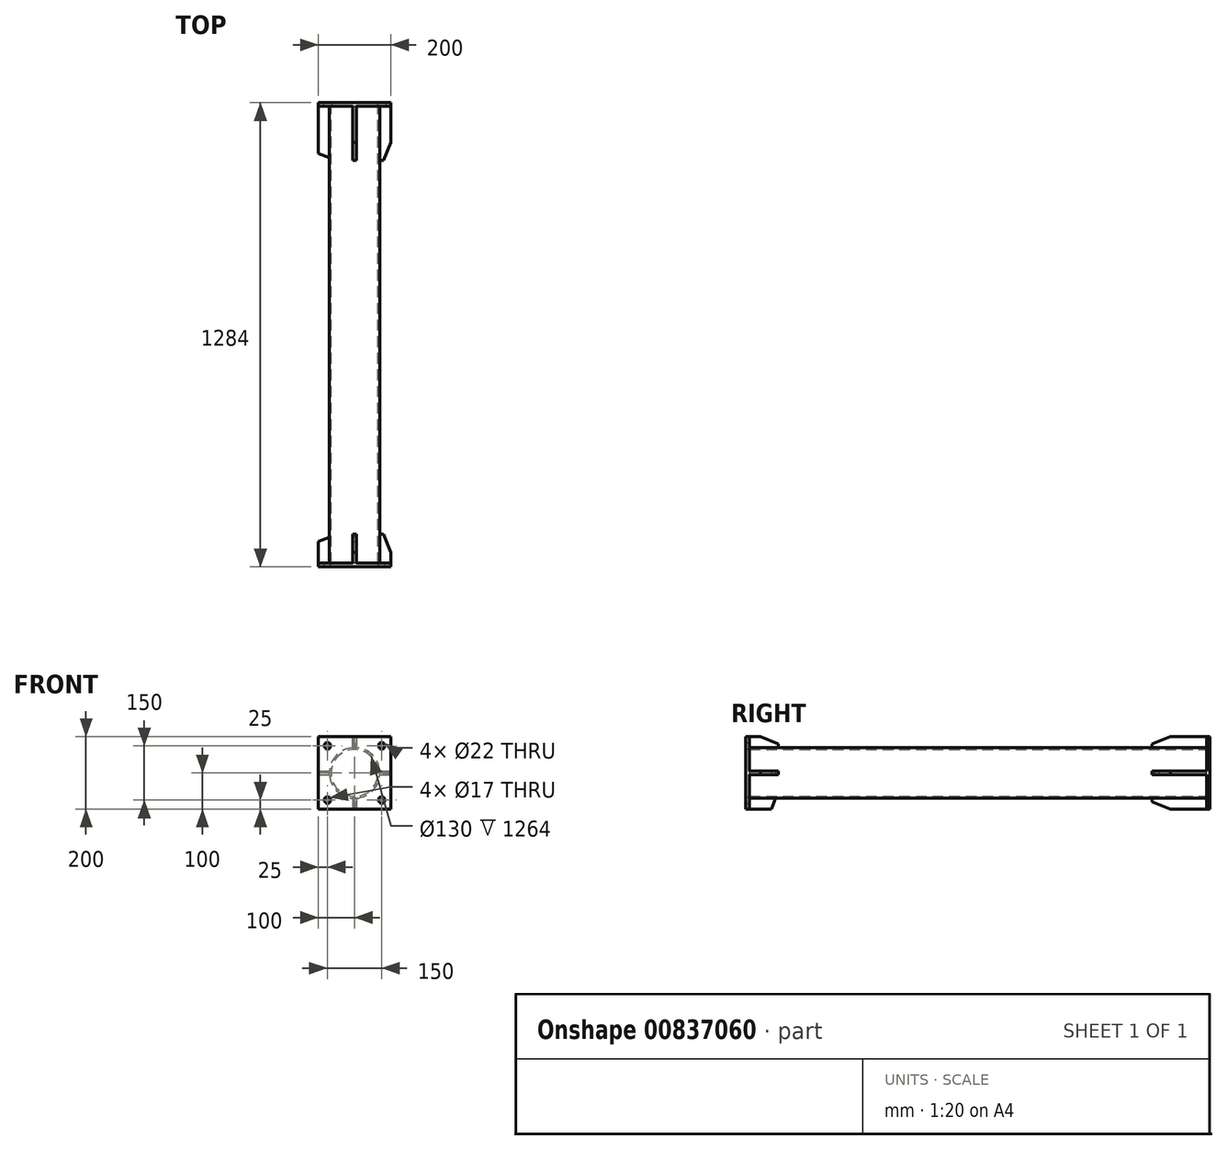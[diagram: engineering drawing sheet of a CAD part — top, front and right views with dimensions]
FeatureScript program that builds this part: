
annotation { "Feature Type Name" : "Feature", "Feature Type Description" : "" }
export const myFeature = defineFeature(function(context is Context, id is Id, definition is map)
    precondition{}
    {
        {
            var Q0;
            Q0=qCreatedBy(makeId("Front.planeOp"),FACE);
            var sketch = newSketch(context, id + "F0", { "sketchPlane" : qUnion([Q0])});
            skCircle(sketch, "E0", {"center": v(0, 0) * mm, "radius": 70 * mm});
            skCircle(sketch, "E1", {"center": v(0, 0) * mm, "radius": 65 * mm});
            skSolve(sketch);
        }
        {
            var Q0;
            Q0=qSketchRegion(id+"F0",true);
            extrude(context, id + "F1", {"entities" : qUnion([Q0]), "depth" : 1264 * mm, "offsetDistance" : 25 * mm});
        }
        {
            var Q0;
            Q0=qCreatedBy(makeId("Front.planeOp"),FACE);
            var sketch = newSketch(context, id + "F2", { "sketchPlane" : qUnion([Q0])});
            skLineSegment(sketch, "E2.bottom", {"start": v(-100, 100) * mm, "end": v(100, 100) * mm});
            skLineSegment(sketch, "E2.top", {"start": v(-100, -100) * mm, "end": v(100, -100) * mm});
            skLineSegment(sketch, "E2.left", {"start": v(-100, 100) * mm, "end": v(-100, -100) * mm});
            skLineSegment(sketch, "E2.right", {"start": v(100, 100) * mm, "end": v(100, -100) * mm});
            skLineSegment(sketch, "E3", {"start": v(-100, 0) * mm, "end": v(100, 0) * mm, "construction": true});
            skLineSegment(sketch, "E4", {"start": v(0, 100) * mm, "end": v(0, -100) * mm, "construction": true});
            skCircle(sketch, "E5", {"center": v(-75, 75) * mm, "radius": 11 * mm});
            skCircle(sketch, "E6.MirrorC", {"center": v(-75, -75) * mm, "radius": 11 * mm});
            skCircle(sketch, "E7.MirrorC", {"center": v(75, 75) * mm, "radius": 11 * mm});
            skCircle(sketch, "E8.MirrorC", {"center": v(75, -75) * mm, "radius": 11 * mm});
            skSolve(sketch);
        }
        {
            var Q0;
            Q0=qSketchRegion(id+"F2",true);
            extrude(context, id + "F3", {"entities" : qUnion([Q0]), "operationType" : NewBodyOperationType.ADD, "oppositeDirection" : true, "depth" : 10 * mm, "offsetDistance" : 25 * mm});
        }
        {
            var Q0;
            Q0=qCreatedBy(makeId("Front.planeOp"),FACE);
            var sketch = newSketch(context, id + "F4", { "sketchPlane" : qUnion([Q0])});
            skLineSegment(sketch, "E9.bottom", {"start": v(-100, 5) * mm, "end": v(-69.82, 5) * mm});
            skLineSegment(sketch, "E9.top", {"start": v(-100, -5) * mm, "end": v(-69.82, -5) * mm});
            skLineSegment(sketch, "E9.left", {"start": v(-100, 5) * mm, "end": v(-100, -5) * mm});
            skLineSegment(sketch, "E9.right", {"start": v(-69.82, 5) * mm, "end": v(-69.82, -5) * mm});
            skLineSegment(sketch, "E10.bottom", {"start": v(-5, 69.82) * mm, "end": v(5, 69.82) * mm});
            skLineSegment(sketch, "E10.top", {"start": v(-5, 100) * mm, "end": v(5, 100) * mm});
            skLineSegment(sketch, "E10.left", {"start": v(-5, 69.82) * mm, "end": v(-5, 100) * mm});
            skLineSegment(sketch, "E10.right", {"start": v(5, 69.82) * mm, "end": v(5, 100) * mm});
            skLineSegment(sketch, "E11.bottom", {"start": v(69.82, 5) * mm, "end": v(100, 5) * mm});
            skLineSegment(sketch, "E11.top", {"start": v(69.82, -5) * mm, "end": v(100, -5) * mm});
            skLineSegment(sketch, "E11.left", {"start": v(69.82, 5) * mm, "end": v(69.82, -5) * mm});
            skLineSegment(sketch, "E11.right", {"start": v(100, 5) * mm, "end": v(100, -5) * mm});
            skLineSegment(sketch, "E12.bottom", {"start": v(5, -69.82) * mm, "end": v(-5, -69.82) * mm});
            skLineSegment(sketch, "E12.top", {"start": v(5, -100) * mm, "end": v(-5, -100) * mm});
            skLineSegment(sketch, "E12.left", {"start": v(5, -69.82) * mm, "end": v(5, -100) * mm});
            skLineSegment(sketch, "E12.right", {"start": v(-5, -69.82) * mm, "end": v(-5, -100) * mm});
            skSolve(sketch);
        }
        {
            var Q0;
            Q0=qSketchRegion(id+"F4",true);
            extrude(context, id + "F5", {"entities" : qUnion([Q0]), "operationType" : NewBodyOperationType.ADD, "depth" : 150 * mm, "offsetDistance" : 25 * mm});
        }
        {
            var Q0;
            Q0=makeQuery(id+"F5.opExtrude","CAP_EDGE",EDGE,{"disambiguationData":[OSD([sQuery(id+"F4.wireOp",EDGE,"E9.left")])],"isStart":false});
            var Q1;
            Q1=makeQuery(id+"F5.opExtrude","CAP_EDGE",EDGE,{"disambiguationData":[OSD([sQuery(id+"F4.wireOp",EDGE,"E10.top")])],"isStart":false});
            var Q2;
            Q2=makeQuery(id+"F5.opExtrude","CAP_EDGE",EDGE,{"disambiguationData":[OSD([sQuery(id+"F4.wireOp",EDGE,"E12.top")])],"isStart":false});
            var Q3;
            Q3=makeQuery(id+"F5.opExtrude","CAP_EDGE",EDGE,{"disambiguationData":[OSD([sQuery(id+"F4.wireOp",EDGE,"E11.right")])],"isStart":false});
            chamfer(context, id + "F6", {"entities" : qUnion([Q0, Q1, Q2, Q3]), "chamferType" : ChamferType.TWO_OFFSETS, "width1" : 50 * mm, "oppositeDirection" : false, "width2" : 20 * mm});
        }
        {
            var Q0;
            Q0=makeQuery(id+"F1.opExtrude","CAP_FACE",FACE,{"disambiguationData":[OSD([sQuery(id+"F0.wireOp",EDGE,"E0"),sQuery(id+"F0.wireOp",EDGE,"E1")])],"isStart":false});
            cPlane(context, id + "F7", {"entities" : qUnion([Q0]), "cplaneType" : CPlaneType.OFFSET, "offset" : 0 * mm, "width" : 150 * mm, "height" : 150 * mm});
        }
        {
            var Q0;
            Q0=qCreatedBy(id+"F7.planeOp",FACE);
            var sketch = newSketch(context, id + "F8", { "sketchPlane" : qUnion([Q0])});
            skLineSegment(sketch, "E13.bottom", {"start": v(-100, 100) * mm, "end": v(100, 100) * mm});
            skLineSegment(sketch, "E13.top", {"start": v(-100, -100) * mm, "end": v(100, -100) * mm});
            skLineSegment(sketch, "E13.left", {"start": v(-100, 100) * mm, "end": v(-100, -100) * mm});
            skLineSegment(sketch, "E13.right", {"start": v(100, 100) * mm, "end": v(100, -100) * mm});
            skCircle(sketch, "E14", {"center": v(-75, 75) * mm, "radius": 8.5 * mm});
            skCircle(sketch, "E15.MirrorC", {"center": v(75, 75) * mm, "radius": 8.5 * mm});
            skLineSegment(sketch, "E16", {"start": v(-100, 0) * mm, "end": v(100, 0) * mm, "construction": true});
            skLineSegment(sketch, "E17", {"start": v(0, 100) * mm, "end": v(0, -100) * mm, "construction": true});
            skCircle(sketch, "E18.MirrorC", {"center": v(-75, -75) * mm, "radius": 8.5 * mm});
            skCircle(sketch, "E19.MirrorC", {"center": v(75, -75) * mm, "radius": 8.5 * mm});
            skSolve(sketch);
        }
        {
            var Q0;
            Q0=qSketchRegion(id+"F8",true);
            extrude(context, id + "F9", {"entities" : qUnion([Q0]), "operationType" : NewBodyOperationType.ADD, "depth" : 10 * mm, "offsetDistance" : 25 * mm});
        }
        {
            var Q0;
            {var subQ0=sQuery(id+"F8.wireOp",EDGE,"E13.left");var subQ1=sQuery(id+"F8.wireOp",EDGE,"E13.top");var subQ2=sQuery(id+"F8.wireOp",EDGE,"E13.bottom");var subQ3=sQuery(id+"F8.wireOp",EDGE,"E13.right");var subQ4=sQuery(id+"F8.wireOp",EDGE,"E14");var subQ5=sQuery(id+"F8.wireOp",EDGE,"E15.MirrorC");var subQ6=sQuery(id+"F8.wireOp",EDGE,"E18.MirrorC");var subQ7=sQuery(id+"F8.wireOp",EDGE,"E19.MirrorC");Q0=makeQuery(id+"F9.boolean.opBoolean","SPLIT",FACE,{"disambiguationData":[TD([makeQuery(id+"F1.opExtrude","SWEPT_FACE",FACE,{"disambiguationData":[OSD([sQuery(id+"F0.wireOp",EDGE,"E0")])]})])],"derivedFrom":makeQuery(id+"F9.opExtrude","CAP_FACE",FACE,{"disambiguationData":[OSD([subQ2,subQ1,subQ0,subQ3,subQ4,subQ5,subQ6,subQ7])],"isStart":true})});}
            var sketch = newSketch(context, id + "F10", { "sketchPlane" : qUnion([Q0])});
            skLineSegment(sketch, "E20.bottom", {"start": v(5, 100) * mm, "end": v(-5, 100) * mm});
            skLineSegment(sketch, "E20.top", {"start": v(5, 69.82) * mm, "end": v(-5, 69.82) * mm});
            skLineSegment(sketch, "E20.left", {"start": v(5, 100) * mm, "end": v(5, 69.82) * mm});
            skLineSegment(sketch, "E20.right", {"start": v(-5, 100) * mm, "end": v(-5, 69.82) * mm});
            skLineSegment(sketch, "E21.bottom", {"start": v(100, 5) * mm, "end": v(69.82, 5) * mm});
            skLineSegment(sketch, "E21.top", {"start": v(100, -5) * mm, "end": v(69.82, -5) * mm});
            skLineSegment(sketch, "E21.left", {"start": v(100, 5) * mm, "end": v(100, -5) * mm});
            skLineSegment(sketch, "E21.right", {"start": v(69.82, 5) * mm, "end": v(69.82, -5) * mm});
            skLineSegment(sketch, "E22.bottom", {"start": v(-5, -69.82) * mm, "end": v(5, -69.82) * mm});
            skLineSegment(sketch, "E22.top", {"start": v(-5, -100) * mm, "end": v(5, -100) * mm});
            skLineSegment(sketch, "E22.left", {"start": v(-5, -69.82) * mm, "end": v(-5, -100) * mm});
            skLineSegment(sketch, "E22.right", {"start": v(5, -69.82) * mm, "end": v(5, -100) * mm});
            skLineSegment(sketch, "E23.bottom", {"start": v(-69.82, -5) * mm, "end": v(-100, -5) * mm});
            skLineSegment(sketch, "E23.top", {"start": v(-69.82, 5) * mm, "end": v(-100, 5) * mm});
            skLineSegment(sketch, "E23.left", {"start": v(-69.82, -5) * mm, "end": v(-69.82, 5) * mm});
            skLineSegment(sketch, "E23.right", {"start": v(-100, -5) * mm, "end": v(-100, 5) * mm});
            skSolve(sketch);
        }
        {
            var Q0;
            Q0=qSketchRegion(id+"F10",true);
            extrude(context, id + "F11", {"entities" : qUnion([Q0]), "operationType" : NewBodyOperationType.ADD, "depth" : 80 * mm, "offsetDistance" : 25 * mm});
        }
        {
            var Q0;
            Q0=makeQuery(id+"F11.opExtrude","CAP_EDGE",EDGE,{"disambiguationData":[OSD([sQuery(id+"F10.wireOp",EDGE,"E21.left")])],"isStart":false});
            var Q1;
            Q1=makeQuery(id+"F11.opExtrude","CAP_EDGE",EDGE,{"disambiguationData":[OSD([sQuery(id+"F10.wireOp",EDGE,"E22.top")])],"isStart":false});
            var Q2;
            Q2=makeQuery(id+"F11.opExtrude","CAP_EDGE",EDGE,{"disambiguationData":[OSD([sQuery(id+"F10.wireOp",EDGE,"E20.bottom")])],"isStart":false});
            var Q3;
            Q3=makeQuery(id+"F11.opExtrude","CAP_EDGE",EDGE,{"disambiguationData":[OSD([sQuery(id+"F10.wireOp",EDGE,"E23.right")])],"isStart":false});
            chamfer(context, id + "F12", {"entities" : qUnion([Q0, Q1, Q2, Q3]), "chamferType" : ChamferType.TWO_OFFSETS, "width1" : 20 * mm, "oppositeDirection" : false, "width2" : 50 * mm});
        }
    });
